FCSTD DOCUMENT  (FreeCAD 0.19R)
Label: lerx6
License: All rights reserved
LicenseURL: http://en.wikipedia.org/wiki/All_rights_reserved
objects: Sketcher::SketchObject×3
note: 3 computed .brp shape members not serialized (recipe doc carries the construction recipe); baked Part::Feature solids carry a one-line shape summary decoded from their .brp

FEATURE [Sketcher::SketchObject] Sketch  label="fuselage + wing"
  FullyConstrained = true
  sketch-geometry (9):
    g0: LineSegment StartX=0 StartY=0 StartZ=0 EndX=1000 EndY=0 EndZ=0
    g1: LineSegment StartX=0 StartY=0 StartZ=0 EndX=1000 EndY=1191.75 EndZ=0
    g2: LineSegment StartX=0 StartY=-5 StartZ=0 EndX=1000 EndY=-5 EndZ=0
    g3: LineSegment StartX=0 StartY=-30 StartZ=0 EndX=-970.66 EndY=-30 EndZ=0
    g4: LineSegment StartX=0 StartY=-5 StartZ=0 EndX=0 EndY=-30 EndZ=0
    g5: LineSegment StartX=-970.66 StartY=-30 StartZ=0 EndX=-970.66 EndY=-530 EndZ=0
    g6: LineSegment StartX=-970.66 StartY=-530 StartZ=0 EndX=1000 EndY=-530 EndZ=0
    g7: LineSegment StartX=1000 StartY=-5 StartZ=0 EndX=1000 EndY=-530 EndZ=0
    g8: LineSegment StartX=1000 StartY=1191.75 StartZ=0 EndX=1000 EndY=0 EndZ=0
  constraints (26):
    c: Coincident(g0,g-1)
    c: PointOnObject(g0,g-1)
    c: Distance(g0) = 1000  'wing-root'
    c: Coincident(g1,g0)
    c: Angle(g0,g1) = 0.872665  'LE-sweep'
    c: Vertical(g1,g0)
    c: PointOnObject(g2,g-2)
    c: Horizontal(g2)
    c: Equal(g2,g0)
    c: Distance(g2,g0) = 5
    c: PointOnObject(g3,g-2)
    c: Horizontal(g3)
    c: Distance(g2,g3) = 25
    c: Coincident(g4,g2)
    c: Coincident(g4,g3)
    c: Distance(g3) = 970.66
    c: Coincident(g5,g3)
    c: Vertical(g5)
    c: Distance(g5) = 500
    c: Coincident(g6,g5)
    c: Horizontal(g6)
    c: Vertical(g2,g6)
    c: Coincident(g7,g2)
    c: Coincident(g7,g6)
    c: Coincident(g8,g1)
    c: Coincident(g8,g0)
FEATURE [Sketcher::SketchObject] Sketch001  label="lerx"
  ExternalGeometry = -> [Sketch]
  FullyConstrained = true
  sketch-geometry (10):
    g0: LineSegment StartX=-970.66 StartY=-40 StartZ=0 EndX=-970.56 EndY=-40 EndZ=0
    g1: LineSegment StartX=0 StartY=-40 StartZ=0 EndX=-65.173 EndY=-40 EndZ=0
    g2: LineSegment StartX=-970.56 StartY=-40 StartZ=0 EndX=-65.173 EndY=-40 EndZ=0
    g3: LineSegment StartX=-970.56 StartY=-40 StartZ=0 EndX=-970.56 EndY=360 EndZ=0
    g4: LineSegment StartX=191.633 StartY=276.05 StartZ=0 EndX=171.633 EndY=276.05 EndZ=0
    g5: LineSegment StartX=191.633 StartY=276.05 StartZ=0 EndX=-65.173 EndY=-30 EndZ=0
    g6: GeomPoint X=-970.56 Y=-30 Z=0
    g7: LineSegment StartX=171.633 StartY=276.05 StartZ=0 EndX=-970.56 EndY=-30 EndZ=0
    g8: GeomPoint X=-517.916 Y=-40 Z=0
    g9: GeomPoint X=231.633 Y=276.05 Z=0
  constraints (30):
    c: Horizontal(g0)
    c: Vertical(g0,g-3)
    c: Distance(g0) = 0.1
    c: Distance(g0,g-3) = 10
    c: PointOnObject(g1,g-2)
    c: Horizontal(g1)
    c: Horizontal(g1,g0)
    c: Coincident(g2,g0)
    c: Coincident(g2,g1)
    c: Coincident(g3,g0)
    c: Vertical(g3)
    c: Horizontal(g4)
    c: Distance(g4) = 20
    c: Distance(g3) = 400
    c: Coincident(g5,g4)
    c: PointOnObject(g5,g-3)
    c: Vertical(g5,g1)
    c: Parallel(g-4,g5)
    c: DistanceY(g5,g4) = 306.05
    c: PointOnObject(g6,g-3)
    c: Vertical(g6,g0)
    c: Coincident(g7,g4)
    c: Coincident(g7,g6)
    c: Angle(g7,g3) = 1.309
    c: Distance(g7,g5) = 905.387
    c: Symmetric(g0,g1,g8)
    c: Distance(g8,g1) = 452.744
    c: PointOnObject(g9,g-4)
    c: Horizontal(g9,g4)
    c: Distance(g9,g4) = 40
FEATURE [Sketcher::SketchObject] Sketch002
  ExternalGeometry = -> [Sketch,Sketch001]
  FullyConstrained = true
  sketch-geometry (3):
    g0: LineSegment StartX=-65.173 StartY=470 StartZ=0 EndX=-969.319 EndY=517.384 EndZ=0
    g1: LineSegment StartX=-970.56 StartY=-30 StartZ=0 EndX=-65.173 EndY=-30 EndZ=0
    g2: LineSegment StartX=-65.173 StartY=470 StartZ=0 EndX=-970.56 EndY=470 EndZ=0
  constraints (11):
    c: Vertical(g-4,g0)
    c: Coincident(g1,g-5)
    c: Coincident(g1,g-4)
    c: Equal(g1,g0)
    c: Coincident(g2,g0)
    c: Horizontal(g2)
    c: Vertical(g1,g2)
    c: DistanceY(g2,g0) = 47.3843
    c: DistanceX(g2,g0) = 1.2408
    c: Angle(g0,g2) = 0.0523599
    c: DistanceY(g0,g1) = -500
